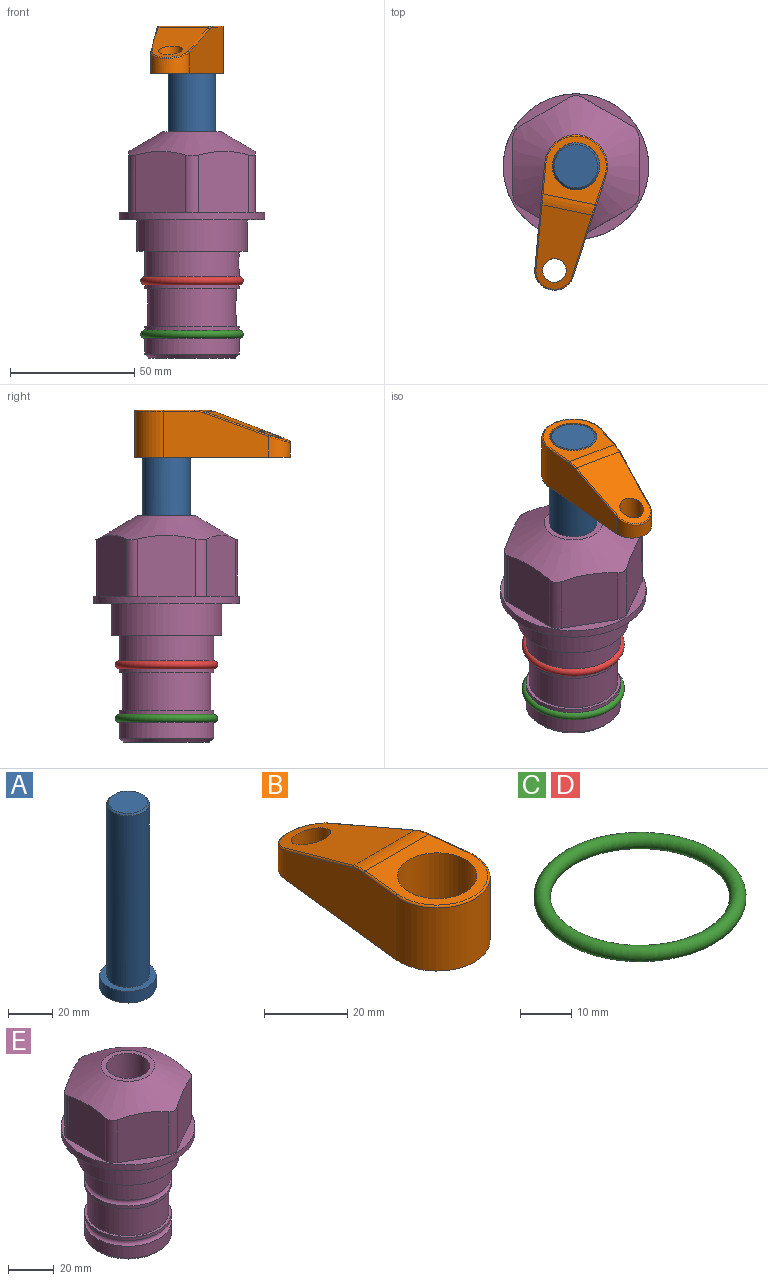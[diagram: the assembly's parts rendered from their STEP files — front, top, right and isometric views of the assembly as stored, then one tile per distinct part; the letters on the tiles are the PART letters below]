
ASSEMBLY  parts=5 mates=3
PART A: 6 faces, bbox 25.4x25.4x101.6 mm
  f0: plane 17.46x17.46mm, normal (0,0,1), area 239.5mm2, adj f5
  f1: plane 25.4x25.4mm, normal (0,0,-1), area 506.7mm2, adj f2
  f2: cylinder r=12.7mm len=25.4mm, axis (0,0,1), area 506.7mm2, adj f1,f3
  f3: plane 25.4x25.4mm, normal (0,0,1), area 221.7mm2, adj f2,f4
  f4: cylinder r=9.53mm len=94.46mm, axis (0,0,1), area 5653mm2, adj f3,f5
  f5: cone r=8.73mm half-angle=45deg, axis (0,0,-1), area 64.4mm2, adj f0,f4
PART B: 44 faces, bbox 27.5x64.5x19.1 mm
  f0: plane 2.3x0.95mm, normal (0,0,-1), area 1mm2, adj f25,f30,f34
  f1: plane 63.5x25.4mm, normal (0,0,-1), area 561.7mm2, adj f2,f3,f4,f5,f6,f7,f19,f20
  f2: cylinder r=12.7mm len=25.4mm, axis (0,0,-1), area 792.2mm2, adj f1,f3,f5,f13
  f3: plane 42.33x18.54mm, normal (0.99,0.11,0), area 647mm2, adj f1,f2,f4,f11,f12,f14
  f4: cylinder r=7.94mm len=15.78mm, axis (0,0,-1), area 158.6mm2, adj f1,f3,f5,f16
  f5: plane 42.33x18.54mm, normal (-0.99,0.11,0), area 647mm2, adj f1,f2,f4,f15,f17,f18
  f6: cylinder r=9.53mm len=19.05mm, axis (0,0,-1), area 1140.1mm2, adj f1,f8
  f7: cylinder r=4.76mm len=10.98mm, axis (0,0,-1), area 276.1mm2, adj f1,f9
  f8: plane 25.83x24.38mm, normal (0,0,1), area 262.2mm2, adj f6,f10,f11,f13,f15
  f9: plane 32.49x20.55mm, normal (0,0.34,0.94), area 489.9mm2, adj f7,f10,f14,f16,f18
  f10: cylinder r=12.7mm len=21.49mm, axis (-1,0,0), area 93.2mm2, adj f8,f9,f12,f17
  f11: cylinder r=0.51mm len=12.34mm, axis (0.11,-0.99,0), area 9.9mm2, adj f3,f8,f12,f13
  f12: bspline ~7.62x1.64mm, area 3.5mm2, adj f3,f10,f11,f14
  f13: torus R=12.19mm, axis (0,0,1), area 33.6mm2, adj f2,f8,f11,f15
  f14: cylinder r=0.51mm len=26.01mm, axis (0.1,-0.93,0.34), area 21.6mm2, adj f3,f9,f12,f16
  f15: cylinder r=0.51mm len=12.34mm, axis (0.11,0.99,0), area 9.9mm2, adj f5,f8,f13,f17
  f16: bspline ~15.78x7.05mm, area 15.7mm2, adj f4,f9,f14,f18
  f17: bspline ~7.62x1.64mm, area 3.5mm2, adj f5,f10,f15,f18
  f18: cylinder r=0.51mm len=26.01mm, axis (0.1,0.93,-0.34), area 21.6mm2, adj f5,f9,f16,f17
  f19: plane 21.6x14.29mm, normal (-0.99,-0.11,0), area 242.6mm2, adj f1,f26,f28,f34,f36,f38
  f20: plane 21.6x14.29mm, normal (0.99,-0.11,0), area 242.6mm2, adj f1,f27,f29,f37,f39,f41
  f21: cylinder r=12.7mm len=14.29mm, axis (0,0,-1), area 173.2mm2, adj f1,f26,f27,f30,f31,f33
  f22: cylinder r=7.94mm len=7.63mm, axis (0,0,-1), area 53.8mm2, adj f1,f28,f29,f42
  f23: plane 2.3x0.95mm, normal (0,0,-1), area 1mm2, adj f25,f33,f37
  f24: plane 17.94x12.32mm, normal (0,-0.34,-0.94), area 191.2mm2, adj f25,f38,f41,f42
  f25: cylinder r=9.53mm len=12.93mm, axis (-1,0,0), area 37.5mm2, adj f0,f23,f24,f31,f36,f39
  f26: cylinder r=1.59mm len=14.29mm, axis (0,0,-1), area 49mm2, adj f1,f19,f21,f32
  f27: cylinder r=1.59mm len=14.29mm, axis (0,0,-1), area 49mm2, adj f1,f20,f21,f35
  f28: cylinder r=1.59mm len=7.28mm, axis (0,0,-1), area 22.1mm2, adj f1,f19,f22,f40
  f29: cylinder r=1.59mm len=7.28mm, axis (0,0,-1), area 22.1mm2, adj f1,f20,f22,f43
  f30: torus R=14.29mm, axis (0,0,1), area 5.8mm2, adj f0,f21,f31,f32
  f31: bspline ~11.06x2.73mm, area 20.8mm2, adj f21,f25,f30,f33
  f32: sphere r=1.59mm, area 5.4mm2, adj f26,f30,f34
  f33: torus R=14.29mm, axis (0,0,1), area 5.8mm2, adj f21,f23,f31,f35
  f34: cylinder r=1.59mm len=1.68mm, axis (-0.11,0.99,0), area 2.4mm2, adj f0,f19,f32,f36
  f35: sphere r=1.59mm, area 5.4mm2, adj f27,f33,f37
  f36: bspline ~5.82x2.33mm, area 7.7mm2, adj f19,f25,f34,f38
  f37: cylinder r=1.59mm len=1.68mm, axis (0.11,0.99,0), area 2.4mm2, adj f20,f23,f35,f39
  f38: cylinder r=1.59mm len=18.33mm, axis (0.1,-0.93,0.34), area 46.7mm2, adj f19,f24,f36,f40
  f39: bspline ~5.82x2.33mm, area 7.7mm2, adj f20,f25,f37,f41
  f40: sphere r=1.59mm, area 3.6mm2, adj f28,f38,f42
  f41: cylinder r=1.59mm len=18.33mm, axis (0.1,0.93,-0.34), area 46.7mm2, adj f20,f24,f39,f43
  f42: bspline ~8.31x1.84mm, area 15.3mm2, adj f22,f24,f40,f43
  f43: sphere r=1.59mm, area 3.6mm2, adj f29,f41,f42
PART C: 1 faces, bbox 44.7x44.7x3.2 mm
  f0: torus R=19.05mm, axis (0,0,1), area 1193.9mm2
PART D: same geometry as C
PART E: 36 faces, bbox 58.7x58.7x91.2 mm
  f0: cylinder r=17.78mm len=35.56mm, axis (0,0,1), area 1670.8mm2, adj f23,f24,f31
  f1: cylinder r=19.05mm len=38.1mm, axis (0,0,1), area 1191.9mm2, adj f26,f27,f30
  f2: plane 58.66x58.66mm, normal (0,0,-1), area 1150.6mm2, adj f3,f28
  f3: cylinder r=29.33mm len=58.66mm, axis (0,0,-1), area 585.1mm2, adj f2,f4
  f4: plane 58.66x58.66mm, normal (0,0,1), area 475.9mm2, adj f3,f5,f6,f7,f8,f9,f10,f11
  f5: plane 24.5x20.32mm, normal (-0.5,0.87,0), area 562.8mm2, adj f4,f15,f16,f17
  f6: plane 24.5x20.32mm, normal (0.5,0.87,0), area 562.8mm2, adj f4,f14,f15,f17
  f7: plane 24.5x23.48mm, normal (1,0,0), area 562.8mm2, adj f4,f13,f14,f17
  f8: plane 24.5x20.32mm, normal (0.5,-0.87,0), area 562.8mm2, adj f4,f12,f13,f17
  f9: plane 24.5x20.32mm, normal (-0.5,-0.87,0), area 562.8mm2, adj f4,f11,f12,f17
  f10: plane 24.5x23.48mm, normal (-1,0,0), area 562.8mm2, adj f4,f11,f16,f17
  f11: cylinder r=5.08mm len=23.01mm, axis (0,0,-1), area 121.2mm2, adj f4,f9,f10,f17
  f12: cylinder r=5.08mm len=23.01mm, axis (0,0,-1), area 121.2mm2, adj f4,f8,f9,f17
  f13: cylinder r=5.08mm len=23.01mm, axis (0,0,-1), area 121.2mm2, adj f4,f7,f8,f17
  f14: cylinder r=5.08mm len=23.01mm, axis (0,0,-1), area 121.2mm2, adj f4,f6,f7,f17
  f15: cylinder r=5.08mm len=23.01mm, axis (0,0,-1), area 121.2mm2, adj f4,f5,f6,f17
  f16: cylinder r=5.08mm len=23.01mm, axis (0,0,-1), area 121.2mm2, adj f4,f5,f10,f17
  f17: cone r=11.73mm half-angle=60deg, axis (0,0,-1), area 2071.8mm2, adj f5,f6,f7,f8,f9,f10,f11,f12
  f18: plane 23.46x23.46mm, normal (0,0,1), area 147.4mm2, adj f17,f35
  f19: plane 34.93x34.93mm, normal (0,0,-1), area 958mm2, adj f29
  f20: cylinder r=19.05mm len=38.1mm, axis (0,0,1), area 760.1mm2, adj f21,f29
  f21: torus R=19.05mm, axis (0,0,1), area 565.3mm2, adj f20,f22
  f22: cylinder r=19.05mm len=38.1mm, axis (0,0,1), area 190mm2, adj f21,f23
  f23: plane 38.1x38.1mm, normal (0,0,1), area 146.9mm2, adj f0,f22
  f24: plane 38.1x38.1mm, normal (0,0,-1), area 146.9mm2, adj f0,f25
  f25: cylinder r=19.05mm len=38.1mm, axis (0,0,1), area 190mm2, adj f24,f26
  f26: torus R=19.05mm, axis (0,0,1), area 565.3mm2, adj f1,f25
  f27: plane 44.45x44.45mm, normal (0,0,-1), area 411.7mm2, adj f1,f28
  f28: cylinder r=22.23mm len=44.45mm, axis (0,0,1), area 1773.5mm2, adj f2,f27
  f29: cone r=19.05mm half-angle=45deg, axis (0,0,1), area 257.5mm2, adj f19,f20
  f30: cylinder r=3.17mm len=6.75mm, axis (-1,0,0), area 128mm2, adj f1,f33
  f31: cylinder r=3.17mm len=6.35mm, axis (-1,0,0), area 102.5mm2, adj f0,f33
  f32: plane 25.4x25.4mm, normal (0,0,1), area 506.7mm2, adj f33
  f33: cylinder r=12.7mm len=66.42mm, axis (0,0,-1), area 5236.2mm2, adj f30,f31,f32,f34
  f34: cone r=9.53mm half-angle=30deg, axis (0,0,-1), area 443.4mm2, adj f33,f35
  f35: cylinder r=9.53mm len=19.05mm, axis (0,0,-1), area 849mm2, adj f18,f34
PLACE A rot(axis=(0,0,-1),101.7deg) t=(0,0,4.52)mm
PLACE B rot(axis=(0,0,1),168.3deg) t=(0,0,59.13)mm
PLACE C t=(0,0,-21.59)mm
PLACE D at identity
PLACE E at identity fixed
MATE fastened C.f0 <-> E.f0  axis (0,0,1) through (0,0,-46.1)mm
MATE cylindrical A.f2 <-> E.f0  axis (0,0,1) through (0,0,30.16)mm
MATE fastened B.f2 <-> A.f2  axis (0,0,1) through (0,0,78.18)mm
